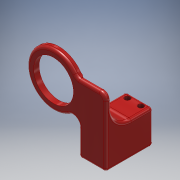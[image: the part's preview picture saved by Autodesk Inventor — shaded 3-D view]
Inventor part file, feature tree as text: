
AUTODESK INVENTOR PART (.ipt)
format: ipt  version: 2018.3 (Build 223284000, 284)  size: 285,184 bytes
history: native  units: mm
features: extrude x6, fillet x6, sketch x6, plane x1
ambient origin geometry x8: Origin, YZ Plane, XZ Plane, XY Plane, X Axis, Y Axis, Z Axis, Center Point
bodies: Solid1 (feature_tree)
feature tree (19):
  extrude  "Extrusion1"  Depth=5.0mm
  plane  "Work Plane1"
  extrude  "Extrusion2"  Depth=4.0mm
  extrude  "Extrusion3"  Depth=19.0mm TaperAngle=0.0deg
  extrude  "Extrusion4"  Depth=5.0mm
  fillet  "Fillet3"  Radius=31.0mm
  fillet  "Fillet4"  Radius=5.0mm
  extrude  "Extrusion5"  Depth=5.0mm
  fillet  "Fillet6"  Radius=4.0mm
  fillet  "Fillet7"  Radius=4.0mm
  fillet  "Fillet8"  Radius=10.0mm
  fillet  "Fillet9"  Radius=10.0mm
  extrude  "Extrusion6"  Depth=5.0mm
  sketch  "Sketch1"  dims[d0=29.5mm d1=5.0mm]
  sketch  "Sketch2"  dims[d2=4.0mm d3=0.0mm d4=50.0mm]
  sketch  "Sketch3"  dims[d5=1.0mm d6=0.0mm d8=19.0mm d9=0.0mm]
  sketch  "Sketch4"  dims[d10=40.0mm d11=15.0mm d12=31.0mm d13=0.0mm d15=5.0mm]
  sketch  "Sketch5"  dims[d16=2.0mm d18=5.0mm d19=4.0mm d20=4.0mm d21=10.0mm d22=10.0mm d23=0.0mm]
  sketch  "Sketch6"  dims[d25=15.0mm d26=5.0mm d27=2.0mm d28=2.0mm d29=4.0mm d30=7.5mm d31=90.0deg d32=4.0mm d33=0.0mm]
